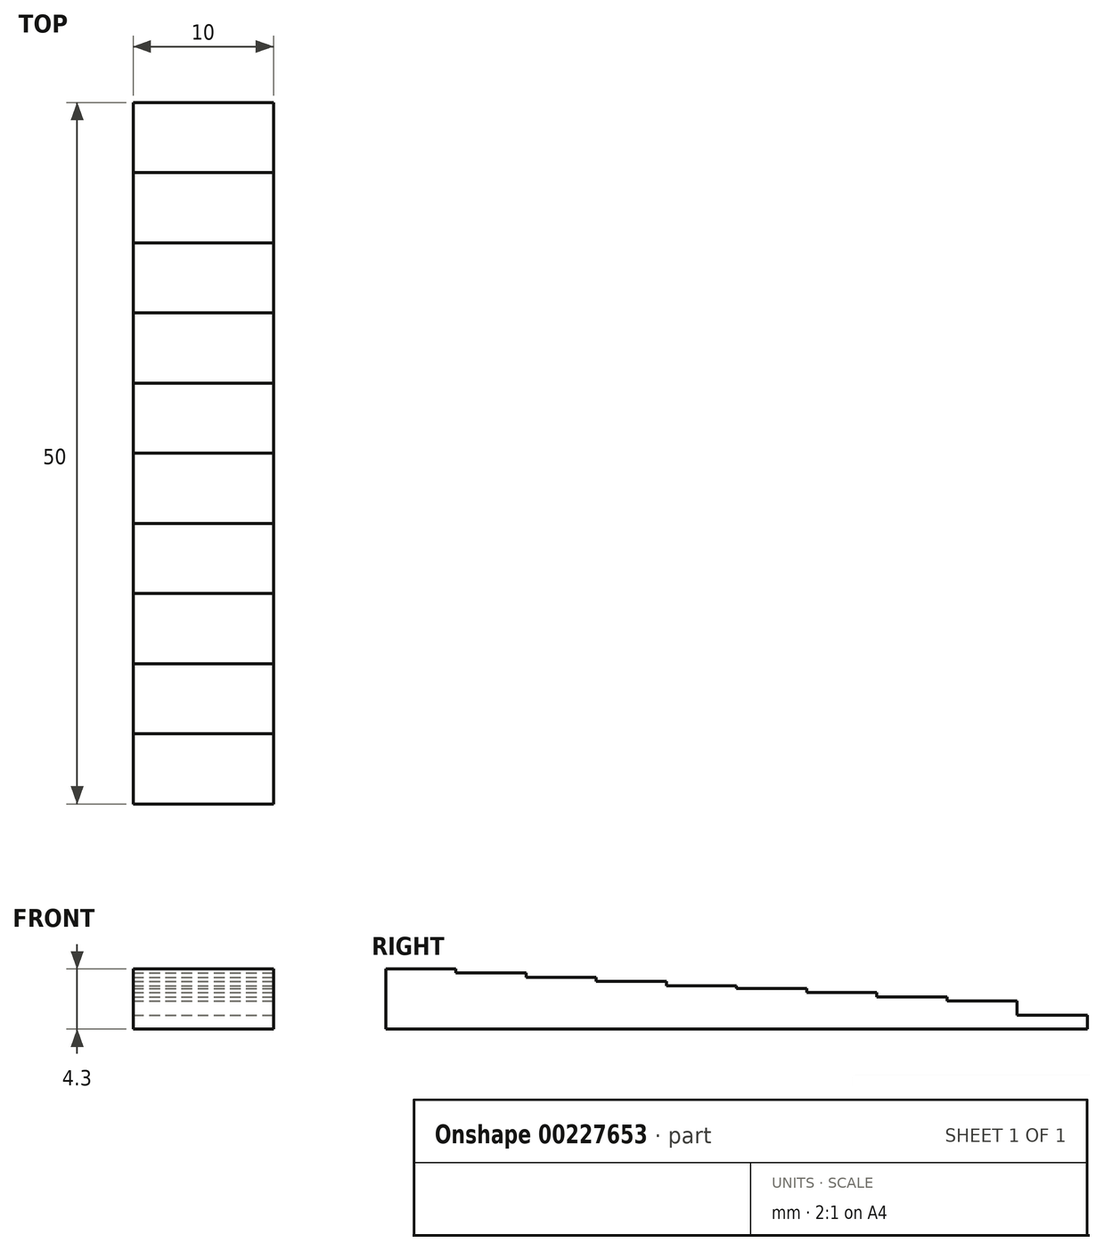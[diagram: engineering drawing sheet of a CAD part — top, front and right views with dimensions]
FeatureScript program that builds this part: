
annotation { "Feature Type Name" : "Feature", "Feature Type Description" : "" }
export const myFeature = defineFeature(function(context is Context, id is Id, definition is map)
    precondition{}
    {
        {
            var Q0;
            Q0=qCreatedBy(makeId("Top.planeOp"),FACE);
            var sketch = newSketch(context, id + "F0", { "sketchPlane" : qUnion([Q0])});
            skLineSegment(sketch, "E0.bottom", {"start": v(-6.21, 37.2) * mm, "end": v(3.79, 37.2) * mm});
            skLineSegment(sketch, "E0.top", {"start": v(-6.21, -12.8) * mm, "end": v(3.79, -12.8) * mm});
            skLineSegment(sketch, "E0.left", {"start": v(-6.21, 37.2) * mm, "end": v(-6.21, -12.8) * mm});
            skLineSegment(sketch, "E0.right", {"start": v(3.79, 37.2) * mm, "end": v(3.79, -12.8) * mm});
            skLineSegment(sketch, "E1", {"start": v(-6.21, 12.2) * mm, "end": v(3.79, 12.2) * mm});
            skLineSegment(sketch, "E2", {"start": v(-1.21, 37.2) * mm, "end": v(-1.21, 32.2) * mm});
            skLineSegment(sketch, "E3", {"start": v(-1.21, 32.2) * mm, "end": v(-1.21, 27.2) * mm});
            skLineSegment(sketch, "E4", {"start": v(-1.21, 27.2) * mm, "end": v(-1.21, 22.2) * mm});
            skLineSegment(sketch, "E5", {"start": v(-1.21, 22.2) * mm, "end": v(-1.21, 17.2) * mm});
            skLineSegment(sketch, "E6", {"start": v(-1.21, 17.2) * mm, "end": v(-1.21, 12.2) * mm});
            skLineSegment(sketch, "E7", {"start": v(-1.21, 12.2) * mm, "end": v(-1.21, 7.2) * mm});
            skLineSegment(sketch, "E8", {"start": v(-1.21, 7.2) * mm, "end": v(-1.21, 2.2) * mm});
            skLineSegment(sketch, "E9", {"start": v(-1.21, 2.2) * mm, "end": v(-1.21, -2.8) * mm});
            skLineSegment(sketch, "E10", {"start": v(-1.21, -2.8) * mm, "end": v(-1.21, -7.8) * mm});
            skLineSegment(sketch, "E11", {"start": v(-1.21, -7.8) * mm, "end": v(-1.21, -12.8) * mm});
            skLineSegment(sketch, "E12", {"start": v(-6.21, 32.2) * mm, "end": v(3.79, 32.2) * mm});
            skLineSegment(sketch, "E13", {"start": v(-6.21, 27.2) * mm, "end": v(3.79, 27.2) * mm});
            skLineSegment(sketch, "E14", {"start": v(-6.21, 22.2) * mm, "end": v(3.79, 22.2) * mm});
            skLineSegment(sketch, "E15", {"start": v(-6.21, 17.2) * mm, "end": v(3.79, 17.2) * mm});
            skLineSegment(sketch, "E16", {"start": v(-6.21, 7.2) * mm, "end": v(3.79, 7.2) * mm});
            skLineSegment(sketch, "E17", {"start": v(-6.21, 2.2) * mm, "end": v(3.79, 2.2) * mm});
            skLineSegment(sketch, "E18", {"start": v(-6.21, -2.8) * mm, "end": v(3.79, -2.8) * mm});
            skLineSegment(sketch, "E19", {"start": v(-6.21, -7.8) * mm, "end": v(3.79, -7.8) * mm});
            skSolve(sketch);
        }
        {
            var Q0;
            {var subQ3=sQuery(id+"F0.wireOp",EDGE,"E2");Q0=makeQuery(id+"F0.imprint","IMPRINT",FACE,{"disambiguationData":[TD([[makeQuery(id+"F0.imprint","IMPRINT",EDGE,{"derivedFrom":subQ3}),-1.0]])]});}
            var Q1;
            {var subQ3=sQuery(id+"F0.wireOp",EDGE,"E2");Q1=makeQuery(id+"F0.imprint","IMPRINT",FACE,{"disambiguationData":[TD([[makeQuery(id+"F0.imprint","IMPRINT",EDGE,{"derivedFrom":subQ3}),1.0]])]});}
            extrude(context, id + "F1", {"entities" : qUnion([Q0, Q1]), "depth" : 1 * mm});
        }
        {
            var Q0;
            {var subQ5=sQuery(id+"F0.wireOp",EDGE,"E3");Q0=makeQuery(id+"F0.imprint","IMPRINT",FACE,{"disambiguationData":[TD([[makeQuery(id+"F0.imprint","IMPRINT",EDGE,{"derivedFrom":subQ5}),-1.0]])]});}
            var Q1;
            {var subQ5=sQuery(id+"F0.wireOp",EDGE,"E3");Q1=makeQuery(id+"F0.imprint","IMPRINT",FACE,{"disambiguationData":[TD([[makeQuery(id+"F0.imprint","IMPRINT",EDGE,{"derivedFrom":subQ5}),1.0]])]});}
            extrude(context, id + "F2", {"entities" : qUnion([Q0, Q1]), "operationType" : NewBodyOperationType.ADD, "depth" : 2 * mm});
        }
        {
            var Q0;
            {var subQ5=sQuery(id+"F0.wireOp",EDGE,"E4");Q0=makeQuery(id+"F0.imprint","IMPRINT",FACE,{"disambiguationData":[TD([[makeQuery(id+"F0.imprint","IMPRINT",EDGE,{"derivedFrom":subQ5}),-1.0]])]});}
            var Q1;
            {var subQ5=sQuery(id+"F0.wireOp",EDGE,"E4");Q1=makeQuery(id+"F0.imprint","IMPRINT",FACE,{"disambiguationData":[TD([[makeQuery(id+"F0.imprint","IMPRINT",EDGE,{"derivedFrom":subQ5}),1.0]])]});}
            extrude(context, id + "F3", {"entities" : qUnion([Q0, Q1]), "operationType" : NewBodyOperationType.ADD, "depth" : 2.3 * mm});
        }
        {
            var Q0;
            {var subQ5=sQuery(id+"F0.wireOp",EDGE,"E5");Q0=makeQuery(id+"F0.imprint","IMPRINT",FACE,{"disambiguationData":[TD([[makeQuery(id+"F0.imprint","IMPRINT",EDGE,{"derivedFrom":subQ5}),1.0]])]});}
            var Q1;
            {var subQ5=sQuery(id+"F0.wireOp",EDGE,"E5");Q1=makeQuery(id+"F0.imprint","IMPRINT",FACE,{"disambiguationData":[TD([[makeQuery(id+"F0.imprint","IMPRINT",EDGE,{"derivedFrom":subQ5}),-1.0]])]});}
            extrude(context, id + "F4", {"entities" : qUnion([Q0, Q1]), "operationType" : NewBodyOperationType.ADD, "depth" : 2.6 * mm});
        }
        {
            var Q0;
            {var subQ5=sQuery(id+"F0.wireOp",EDGE,"E6");Q0=makeQuery(id+"F0.imprint","IMPRINT",FACE,{"disambiguationData":[TD([[makeQuery(id+"F0.imprint","IMPRINT",EDGE,{"derivedFrom":subQ5}),-1.0]])]});}
            var Q1;
            {var subQ5=sQuery(id+"F0.wireOp",EDGE,"E6");Q1=makeQuery(id+"F0.imprint","IMPRINT",FACE,{"disambiguationData":[TD([[makeQuery(id+"F0.imprint","IMPRINT",EDGE,{"derivedFrom":subQ5}),1.0]])]});}
            extrude(context, id + "F5", {"entities" : qUnion([Q0, Q1]), "operationType" : NewBodyOperationType.ADD, "depth" : 2.9 * mm});
        }
        {
            var Q0;
            {var subQ5=sQuery(id+"F0.wireOp",EDGE,"E7");Q0=makeQuery(id+"F0.imprint","IMPRINT",FACE,{"disambiguationData":[TD([[makeQuery(id+"F0.imprint","IMPRINT",EDGE,{"derivedFrom":subQ5}),-1.0]])]});}
            var Q1;
            {var subQ5=sQuery(id+"F0.wireOp",EDGE,"E7");Q1=makeQuery(id+"F0.imprint","IMPRINT",FACE,{"disambiguationData":[TD([[makeQuery(id+"F0.imprint","IMPRINT",EDGE,{"derivedFrom":subQ5}),1.0]])]});}
            extrude(context, id + "F6", {"entities" : qUnion([Q0, Q1]), "operationType" : NewBodyOperationType.ADD, "depth" : 3.1 * mm});
        }
        {
            var Q0;
            {var subQ5=sQuery(id+"F0.wireOp",EDGE,"E8");Q0=makeQuery(id+"F0.imprint","IMPRINT",FACE,{"disambiguationData":[TD([[makeQuery(id+"F0.imprint","IMPRINT",EDGE,{"derivedFrom":subQ5}),-1.0]])]});}
            var Q1;
            {var subQ5=sQuery(id+"F0.wireOp",EDGE,"E8");Q1=makeQuery(id+"F0.imprint","IMPRINT",FACE,{"disambiguationData":[TD([[makeQuery(id+"F0.imprint","IMPRINT",EDGE,{"derivedFrom":subQ5}),1.0]])]});}
            extrude(context, id + "F7", {"entities" : qUnion([Q0, Q1]), "operationType" : NewBodyOperationType.ADD, "depth" : 3.4 * mm});
        }
        {
            var Q0;
            {var subQ5=sQuery(id+"F0.wireOp",EDGE,"E9");Q0=makeQuery(id+"F0.imprint","IMPRINT",FACE,{"disambiguationData":[TD([[makeQuery(id+"F0.imprint","IMPRINT",EDGE,{"derivedFrom":subQ5}),-1.0]])]});}
            var Q1;
            {var subQ5=sQuery(id+"F0.wireOp",EDGE,"E9");Q1=makeQuery(id+"F0.imprint","IMPRINT",FACE,{"disambiguationData":[TD([[makeQuery(id+"F0.imprint","IMPRINT",EDGE,{"derivedFrom":subQ5}),1.0]])]});}
            extrude(context, id + "F8", {"entities" : qUnion([Q0, Q1]), "operationType" : NewBodyOperationType.ADD, "depth" : 3.7 * mm});
        }
        {
            var Q0;
            {var subQ5=sQuery(id+"F0.wireOp",EDGE,"E10");Q0=makeQuery(id+"F0.imprint","IMPRINT",FACE,{"disambiguationData":[TD([[makeQuery(id+"F0.imprint","IMPRINT",EDGE,{"derivedFrom":subQ5}),-1.0]])]});}
            var Q1;
            {var subQ5=sQuery(id+"F0.wireOp",EDGE,"E10");Q1=makeQuery(id+"F0.imprint","IMPRINT",FACE,{"disambiguationData":[TD([[makeQuery(id+"F0.imprint","IMPRINT",EDGE,{"derivedFrom":subQ5}),1.0]])]});}
            extrude(context, id + "F9", {"entities" : qUnion([Q0, Q1]), "operationType" : NewBodyOperationType.ADD, "depth" : 4 * mm});
        }
        {
            var Q0;
            {var subQ3=sQuery(id+"F0.wireOp",EDGE,"E11");Q0=makeQuery(id+"F0.imprint","IMPRINT",FACE,{"disambiguationData":[TD([[makeQuery(id+"F0.imprint","IMPRINT",EDGE,{"derivedFrom":subQ3}),-1.0]])]});}
            var Q1;
            {var subQ3=sQuery(id+"F0.wireOp",EDGE,"E11");Q1=makeQuery(id+"F0.imprint","IMPRINT",FACE,{"disambiguationData":[TD([[makeQuery(id+"F0.imprint","IMPRINT",EDGE,{"derivedFrom":subQ3}),1.0]])]});}
            extrude(context, id + "F10", {"entities" : qUnion([Q0, Q1]), "operationType" : NewBodyOperationType.ADD, "depth" : 4.3 * mm});
        }
    });
